# Revit family: Window_Curtain_Wall-Casement_Outswing-Traco-NX_3100-Architectural
name_source: partatom
category: Windows
revit_build: Autodesk Revit 2015 (Build: 20140905_0730(x64)
units: mm (PartAtom-declared; Revit-internal decimal feet)

## types (1)
- 3 1/4" Frame
    Allowable Air Infiltration Maximum = 0.1 @ 6.2 PSF
    Assembly Code = B2020110
    CTRL Configuration Number = 5
    CTRL Panel Active Frame Width = 0' - 2 1/4"
    CTRL Short Muntin Inset = 0' - 0"
    CTRL Short Munting Visibility = Yes
    Condensation Resistance = 43.0000 psf
    Depth = 0' - 3 1/4"
    Description = Commercial, Casement Outswing Window
    Designation = AAMA/WDMA/CSA 101/I.S.2/A-440-05: C-AW80 And AAMA/WDMA/CSA 101/I.S.2/A-440-08: AW-PG80-C
    Forced Entry Resistance = TYPE B: GRADE 10
    Frame Material = Aluminum - Traco - Anodized - Bronze
    Glazing Configuration = Triple Glazed
    Glazing Material = Glass - Traco - Clear
    Glazing Thickness = 0' - 0 3/4"
    Glazing Type = 3
    Has 1” Insulating Glass Unit = No
    Has Dual Glazing = No
    Has Triple Glazing = Yes
    Head Width = 0' - 3 3/8"
    Height Maximum = 5' - 0"
    Height Minimum = 2' - 6"
    Jamb Width = 0' - 3 3/8"
    Keynote = 08520
    Manufacturer = Traco
    Model = NX-3100
    Panel Configuration = X O-Top
    Product Documentation Link = http://www.alcoa.com
    Product Page URL = http://www.alcoa.com
    Product data url = https://bimobject.com
    Screen Material = Aluminum - Traco - Screen
    Sill Width = 0' - 3 3/8"
    Test Size = 36" X 60"
    Type Comments = From Type Catalog
    U Factor = .43 Per NFRC 100
    URL = http://www.alcoa.com
    Uniform Load Deflection = 80.0000 psf
    Uniform Load Structural = 120.0000 psf
    Water Resistance = 15.0000 psf
    Width Maximum = 8' - 0"
    Width Minimum = 3' - 0"

## geometry (parser evidence)
native form markers: Blend x12, Sweep x20
no freeform markers — native parametric forms only
